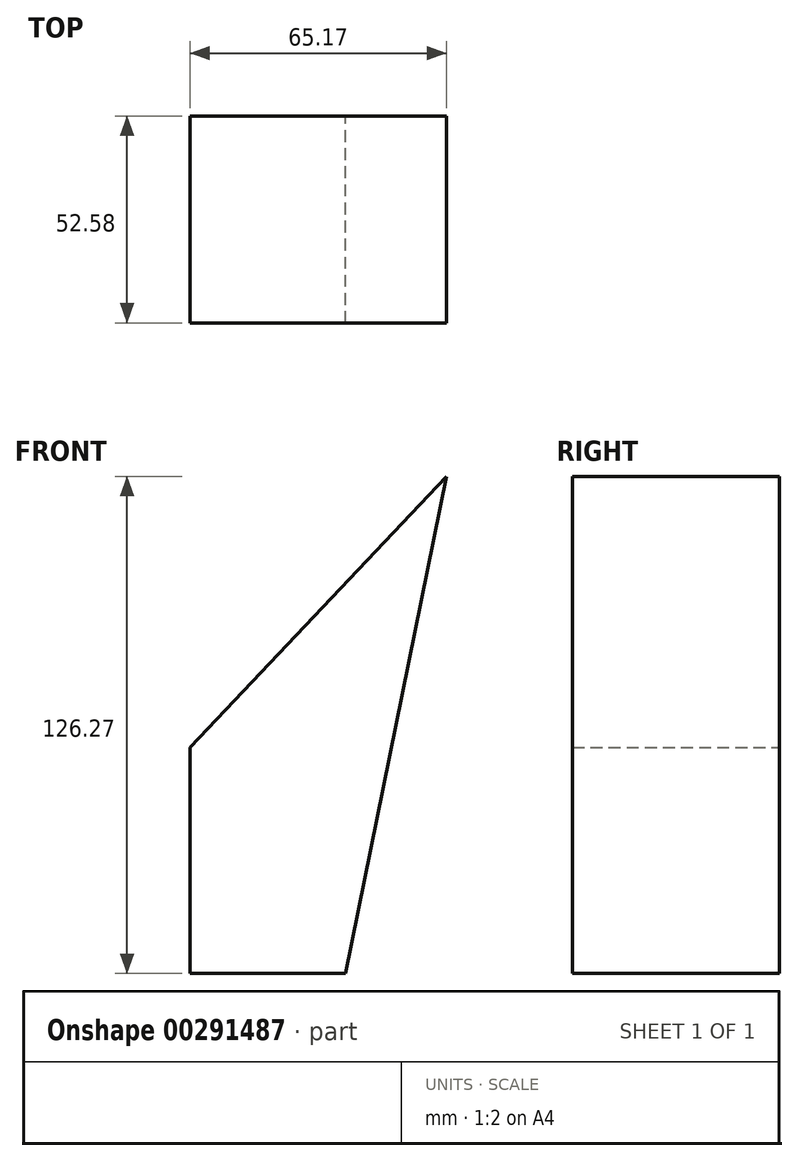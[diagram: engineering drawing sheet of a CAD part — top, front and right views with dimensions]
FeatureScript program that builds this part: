
annotation { "Feature Type Name" : "Feature", "Feature Type Description" : "" }
export const myFeature = defineFeature(function(context is Context, id is Id, definition is map)
    precondition{}
    {
        {
            var Q0;
            Q0=qCreatedBy(makeId("Front.planeOp"),FACE);
            var sketch = newSketch(context, id + "F0", { "sketchPlane" : qUnion([Q0])});
            skLineSegment(sketch, "E0", {"start": v(-10.78, -10.25) * mm, "end": v(-10.78, -67.62) * mm});
            skLineSegment(sketch, "E1", {"start": v(-10.78, -67.62) * mm, "end": v(28.7, -67.62) * mm});
            skLineSegment(sketch, "E2", {"start": v(28.7, -67.62) * mm, "end": v(-10.78, -10.25) * mm});
            skLineSegment(sketch, "E3", {"start": v(-10.78, -10.25) * mm, "end": v(54.4, 58.65) * mm});
            skLineSegment(sketch, "E4", {"start": v(54.4, 58.65) * mm, "end": v(28.7, -67.62) * mm});
            skSolve(sketch);
        }
        {
            var Q0;
            Q0 = qSketchRegion(id + "F0", true);
            extrude(context, id + "F1", {"entities" : qUnion([Q0]), "depth" : 52.58 * mm});
        }
    });
